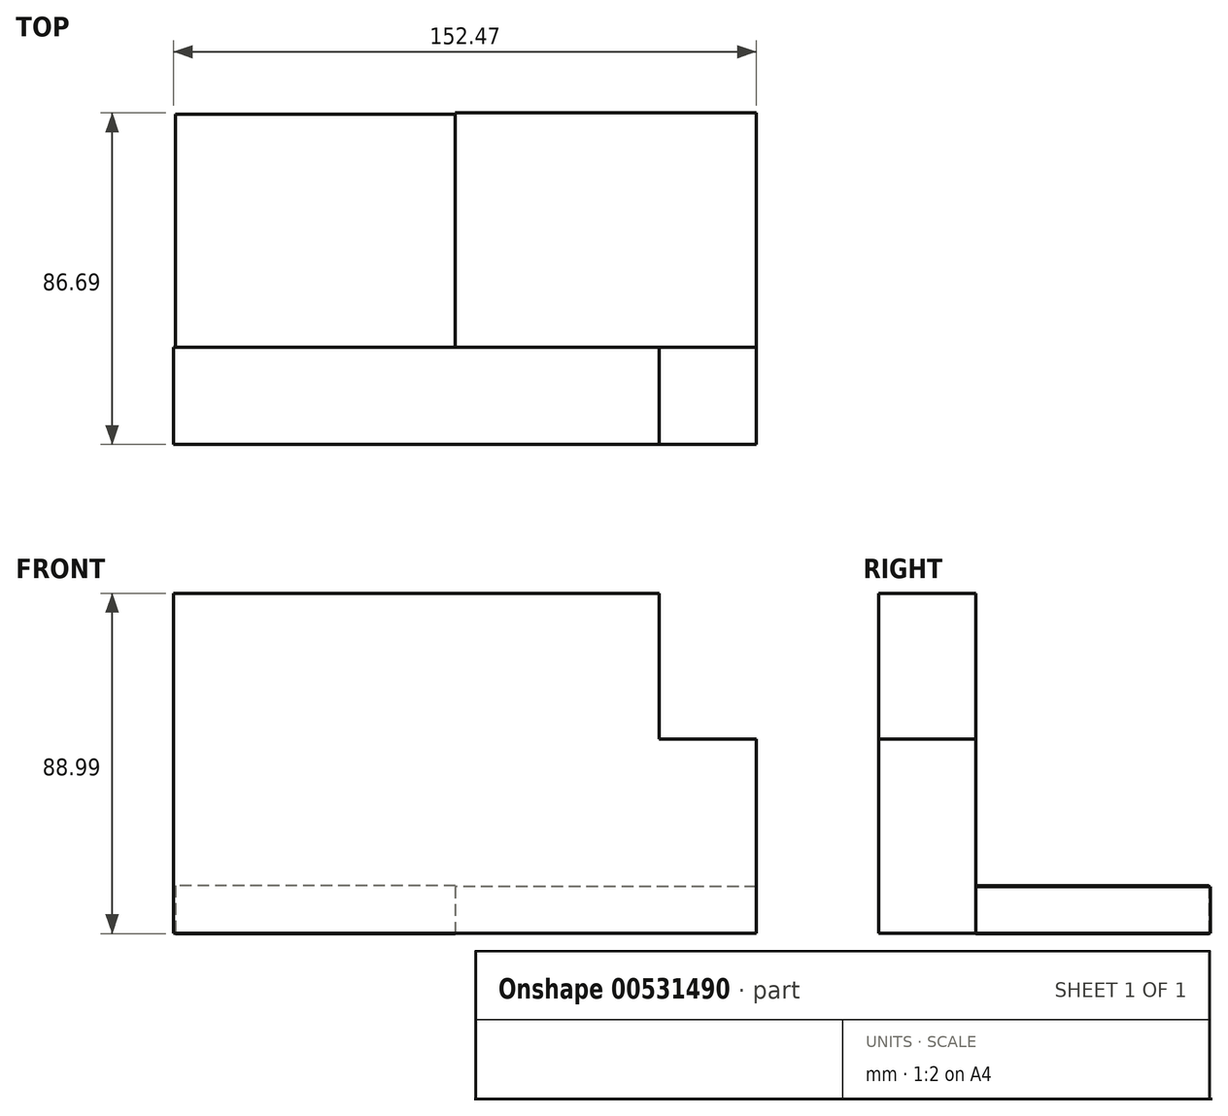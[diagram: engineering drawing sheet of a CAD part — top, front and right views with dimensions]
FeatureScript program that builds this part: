
annotation { "Feature Type Name" : "Feature", "Feature Type Description" : "" }
export const myFeature = defineFeature(function(context is Context, id is Id, definition is map)
    precondition{}
    {
        {
            var Q0;
            Q0=qCreatedBy(makeId("Front.planeOp"),FACE);
            var sketch = newSketch(context, id + "F0", { "sketchPlane" : qUnion([Q0])});
            skLineSegment(sketch, "E0.bottom", {"start": v(-73.73, -18.6) * mm, "end": v(78.67, -18.6) * mm});
            skLineSegment(sketch, "E0.top", {"start": v(-73.73, -69.4) * mm, "end": v(78.67, -69.4) * mm});
            skLineSegment(sketch, "E0.left", {"start": v(-73.73, -18.6) * mm, "end": v(-73.73, -69.4) * mm});
            skLineSegment(sketch, "E0.right", {"start": v(78.67, -18.6) * mm, "end": v(78.67, -69.4) * mm});
            skSolve(sketch);
        }
        {
            var Q0;
            Q0=qCreatedBy(makeId("Front.planeOp"),FACE);
            var sketch = newSketch(context, id + "F1", { "sketchPlane" : qUnion([Q0])});
            skLineSegment(sketch, "E1.bottom", {"start": v(-73.73, -18.6) * mm, "end": v(53.27, -18.6) * mm});
            skLineSegment(sketch, "E1.top", {"start": v(-73.73, 19.5) * mm, "end": v(53.27, 19.5) * mm});
            skLineSegment(sketch, "E1.left", {"start": v(-73.73, -18.6) * mm, "end": v(-73.73, 19.5) * mm});
            skLineSegment(sketch, "E1.right", {"start": v(53.27, -18.6) * mm, "end": v(53.27, 19.5) * mm});
            skSolve(sketch);
        }
        {
            var Q0;
            Q0=makeQuery(id+"F0.imprint","IMPRINT",FACE,{"disambiguationData":[TD([[makeQuery(id+"F0.imprint","IMPRINT",EDGE,{"derivedFrom":sQuery(id+"F0.wireOp",EDGE,"E0.bottom")}),-1.0]])]});
            extrude(context, id + "F2", {"entities" : qUnion([Q0]), "depth" : 25.4 * mm, "offsetDistance" : 25.4 * mm});
        }
        {
            var Q0;
            Q0=makeQuery(id+"F1.imprint","IMPRINT",FACE,{"disambiguationData":[TD([[makeQuery(id+"F1.imprint","IMPRINT",EDGE,{"derivedFrom":sQuery(id+"F1.wireOp",EDGE,"E1.bottom")}),1.0]])]});
            extrude(context, id + "F3", {"entities" : qUnion([Q0]), "operationType" : NewBodyOperationType.ADD, "depth" : 25.4 * mm, "offsetDistance" : 25.4 * mm});
        }
        {
            var Q0;
            Q0=qCreatedBy(makeId("Right.planeOp"),FACE);
            var sketch = newSketch(context, id + "F4", { "sketchPlane" : qUnion([Q0])});
            skLineSegment(sketch, "E2.bottom", {"start": v(0, -57.23) * mm, "end": v(61.29, -57.23) * mm});
            skLineSegment(sketch, "E2.top", {"start": v(0, -69.4) * mm, "end": v(61.29, -69.4) * mm});
            skLineSegment(sketch, "E2.left", {"start": v(0, -57.23) * mm, "end": v(0, -69.4) * mm});
            skLineSegment(sketch, "E2.right", {"start": v(61.29, -57.23) * mm, "end": v(61.29, -69.4) * mm});
            skSolve(sketch);
        }
        {
            var Q0;
            Q0 = qSketchRegion(id + "F4", true);
            extrude(context, id + "F5", {"entities" : qUnion([Q0]), "operationType" : NewBodyOperationType.ADD, "depth" : 78.74 * mm, "offsetDistance" : 25.4 * mm});
        }
        {
            var Q0;
            Q0=qCreatedBy(makeId("Front.planeOp"),FACE);
            var sketch = newSketch(context, id + "F6", { "sketchPlane" : qUnion([Q0])});
            skLineSegment(sketch, "E3.bottom", {"start": v(0, -56.94) * mm, "end": v(-73.17, -56.94) * mm});
            skLineSegment(sketch, "E3.top", {"start": v(0, -69.5) * mm, "end": v(-73.17, -69.5) * mm});
            skLineSegment(sketch, "E3.left", {"start": v(0, -56.94) * mm, "end": v(0, -69.5) * mm});
            skLineSegment(sketch, "E3.right", {"start": v(-73.17, -56.94) * mm, "end": v(-73.17, -69.5) * mm});
            skSolve(sketch);
        }
        {
            var Q0;
            Q0 = qSketchRegion(id + "F6", true);
            extrude(context, id + "F7", {"entities" : qUnion([Q0]), "operationType" : NewBodyOperationType.ADD, "oppositeDirection" : true, "depth" : 60.96 * mm, "offsetDistance" : 25.4 * mm});
        }
    });
